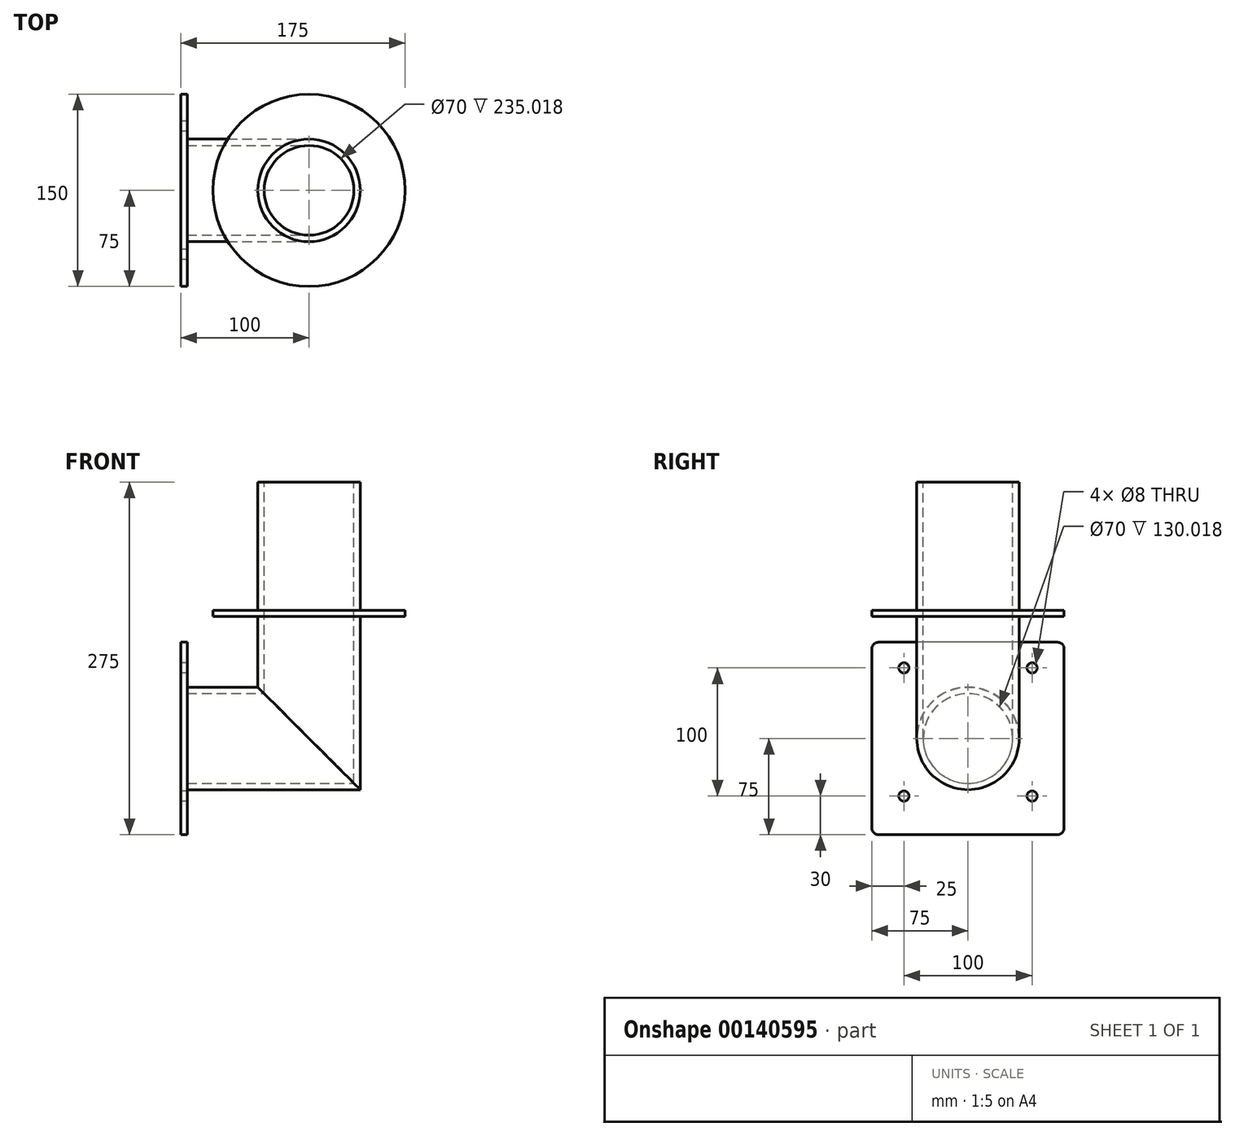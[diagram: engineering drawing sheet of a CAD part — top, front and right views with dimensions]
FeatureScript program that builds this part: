
annotation { "Feature Type Name" : "Feature", "Feature Type Description" : "" }
export const myFeature = defineFeature(function(context is Context, id is Id, definition is map)
    precondition{}
    {
        {
            var Q0;
            Q0=qCreatedBy(makeId("Right.planeOp"),FACE);
            var sketch = newSketch(context, id + "F0", { "sketchPlane" : qUnion([Q0])});
            skCircle(sketch, "E0", {"center": v(0, 0) * mm, "radius": 40 * mm});
            skCircle(sketch, "E1.0", {"center": v(0, 0) * mm, "radius": 35 * mm});
            skSolve(sketch);
        }
        {
            var Q0;
            Q0=qCreatedBy(makeId("Front.planeOp"),FACE);
            var sketch = newSketch(context, id + "F1", { "sketchPlane" : qUnion([Q0])});
            skLineSegment(sketch, "E2.MirrorCS", {"start": v(0, 0) * mm, "end": v(100, 0) * mm});
            skLineSegment(sketch, "E3", {"start": v(100, 0) * mm, "end": v(100, 200) * mm});
            skSolve(sketch);
        }
        {
            var Q0;
            Q0=qCreatedBy(makeId("Right.planeOp"),FACE);
            var sketch = newSketch(context, id + "F2", { "sketchPlane" : qUnion([Q0])});
            skLineSegment(sketch, "E4.bottom", {"start": v(70, -75) * mm, "end": v(-70, -75) * mm});
            skLineSegment(sketch, "E4.top", {"start": v(70, 75) * mm, "end": v(-70, 75) * mm});
            skLineSegment(sketch, "E4.left", {"start": v(75, -70) * mm, "end": v(75, 70) * mm});
            skLineSegment(sketch, "E4.right", {"start": v(-75, -70) * mm, "end": v(-75, 70) * mm});
            skPoint(sketch, "E5.centerSnap0", {"position": v(0, 75) * mm});
            skPoint(sketch, "E6.visualSharp", {"position": v(75, 75) * mm});
            skArc(sketch, "E6.filletArc", {"start": v(75, 70) * mm, "mid": v(73.54, 73.54) * mm, "end": v(70, 75) * mm});
            skPoint(sketch, "E7.visualSharp", {"position": v(-75, 75) * mm});
            skArc(sketch, "E7.filletArc", {"start": v(-70, 75) * mm, "mid": v(-73.54, 73.54) * mm, "end": v(-75, 70) * mm});
            skPoint(sketch, "E8.visualSharp", {"position": v(-75, -75) * mm});
            skArc(sketch, "E8.filletArc", {"start": v(-75, -70) * mm, "mid": v(-73.54, -73.54) * mm, "end": v(-70, -75) * mm});
            skPoint(sketch, "E9.visualSharp", {"position": v(75, -75) * mm});
            skArc(sketch, "E9.filletArc", {"start": v(70, -75) * mm, "mid": v(73.54, -73.54) * mm, "end": v(75, -70) * mm});
            skPoint(sketch, "E10.centerSnap0", {"position": v(-75, 0) * mm});
            skPoint(sketch, "E11.endSnap0", {"position": v(0, -75) * mm});
            skCircle(sketch, "E12.MirrorC", {"center": v(-50, 55) * mm, "radius": 4 * mm});
            skPoint(sketch, "E13.endSnap0", {"position": v(75, 0) * mm});
            skCircle(sketch, "E14.MirrorC", {"center": v(50, 55) * mm, "radius": 4 * mm});
            skCircle(sketch, "E15", {"center": v(-50, -45) * mm, "radius": 4 * mm});
            skCircle(sketch, "E16", {"center": v(50, -45) * mm, "radius": 4 * mm});
            skSolve(sketch);
        }
        {
            var Q0;
            Q0=makeQuery(id+"F0.imprint","IMPRINT",FACE,{"disambiguationData":[TD([[makeQuery(id+"F0.imprint","IMPRINT",EDGE,{"derivedFrom":sQuery(id+"F0.wireOp",EDGE,"E0")}),1.0]])]});
            var Q1;
            Q1=sQuery(id+"F1.wireOp",EDGE,"E2.MirrorCS");
            var Q2;
            Q2=sQuery(id+"F1.wireOp",EDGE,"E3");
            sweep(context, id + "F3", {"profiles" : qUnion([Q0]), "path" : qUnion([Q1, Q2])});
        }
        {
            var Q0;
            Q0=makeQuery(id+"F6.boolean.opBoolean","MERGE",FACE,{"derivedFrom":[makeQuery(id+"F3.opSweep","CAP_FACE",FACE,{"disambiguationData":[OSD([sQuery(id+"F0.wireOp",EDGE,"E0"),sQuery(id+"F0.wireOp",EDGE,"E1.0"),sQuery(id+"F1.wireOp",VERTEX,"E3.end")])],"isStart":false}),makeQuery(id+"F6.opExtrude","CAP_FACE",FACE,{"disambiguationData":[OSD([sQuery(id+"F5.wireOp",EDGE,"E17"),sQuery(id+"F5.wireOp",EDGE,"E18.0")])],"isStart":true})]});
            cPlane(context, id + "F4", {"entities" : qUnion([Q0]), "cplaneType" : CPlaneType.OFFSET, "offset" : 100 * mm, "oppositeDirection" : true, "width" : 150 * mm, "height" : 150 * mm});
        }
        {
            var Q0;
            Q0=qCreatedBy(id+"F4.planeOp",FACE);
            var sketch = newSketch(context, id + "F5", { "sketchPlane" : qUnion([Q0])});
            skCircle(sketch, "E17", {"center": v(100, 0) * mm, "radius": 75 * mm});
            skCircle(sketch, "E18.0", {"center": v(100, 0) * mm, "radius": 40 * mm});
            skSolve(sketch);
        }
        {
            var Q0;
            Q0 = qSketchRegion(id + "F5", true);
            extrude(context, id + "F6", {"entities" : qUnion([Q0]), "operationType" : NewBodyOperationType.ADD, "oppositeDirection" : true, "offsetDistance" : 25 * mm, "depth" : 5 * mm});
        }
        {
            var Q0;
            Q0 = qSketchRegion(id + "F2", true);
            extrude(context, id + "F7", {"entities" : qUnion([Q0]), "operationType" : NewBodyOperationType.ADD, "offsetDistance" : 25 * mm, "depth" : 5 * mm});
        }
    });
